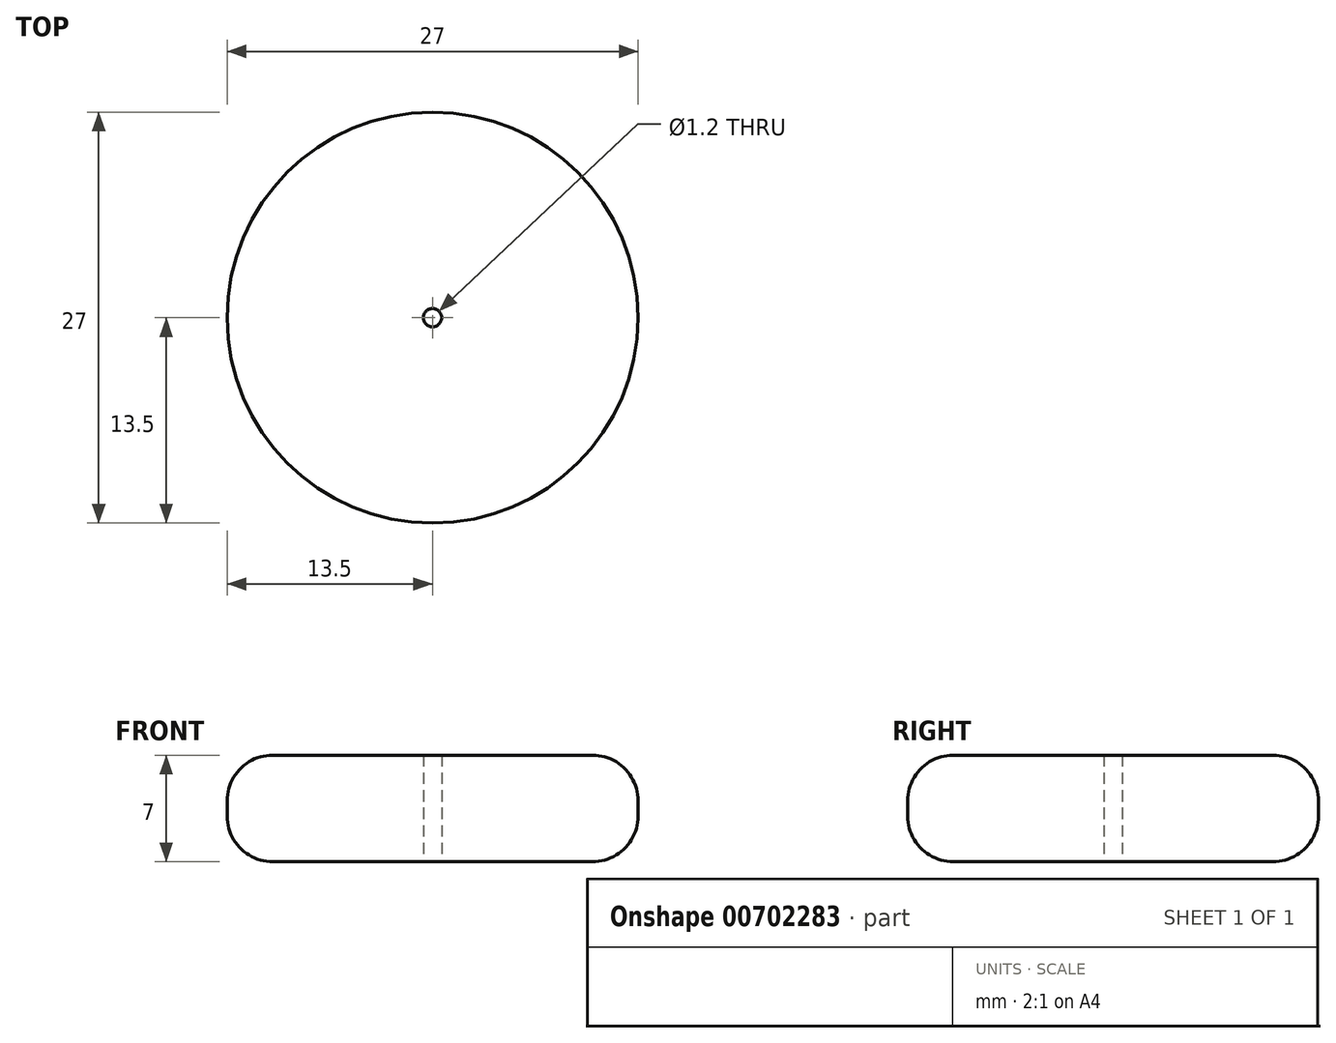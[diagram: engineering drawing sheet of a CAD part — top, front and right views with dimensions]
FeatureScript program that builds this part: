
annotation { "Feature Type Name" : "Feature", "Feature Type Description" : "" }
export const myFeature = defineFeature(function(context is Context, id is Id, definition is map)
    precondition{}
    {
        {
            var Q0;
            Q0=qCreatedBy(makeId("Top.planeOp"),FACE);
            var sketch = newSketch(context, id + "F0", { "sketchPlane" : qUnion([Q0])});
            skCircle(sketch, "E0", {"center": v(0, 0) * mm, "radius": 13.5 * mm});
            skSolve(sketch);
        }
        {
            var Q0;
            Q0 = qSketchRegion(id + "F0", true);
            extrude(context, id + "F1", {"entities" : qUnion([Q0]), "depth" : 7 * mm, "offsetDistance" : 25 * mm});
        }
        {
            var Q0;
            Q0=sQuery(id+"F0.wireOp",VERTEX,"E0.center");
            var Q1;
            Q1=makeQuery(id+"F1.opExtrude","SWEPT_BODY",BODY,{"disambiguationData":[OSD([sQuery(id+"F0.wireOp",EDGE,"E0")])]});
            hole(context, id + "F2", {"style" : HoleStyle.SIMPLE, "endStyle" : HoleEndStyle.THROUGH, "oppositeDirection" : true, "holeDiameter" : 1.2 * mm, "majorDiameter" : 5 * mm, "isTappedThrough" : true, "tappedDepth" : 12 * mm, "tapClearance" : 3, "locations" : qUnion([Q0]), "scope" : qUnion([Q1])});
        }
        {
            var Q0;
            Q0=makeQuery(id+"F1.opExtrude","CAP_EDGE",EDGE,{"disambiguationData":[OSD([sQuery(id+"F0.wireOp",EDGE,"E0")])],"isStart":true});
            var Q1;
            Q1=makeQuery(id+"F1.opExtrude","CAP_EDGE",EDGE,{"disambiguationData":[OSD([sQuery(id+"F0.wireOp",EDGE,"E0")])],"isStart":false});
            fillet(context, id + "F3", {"entities" : qUnion([Q0, Q1]), "radius" : 3 * mm, "tangentPropagation" : true, "allowEdgeOverflow" : false});
        }
    });
